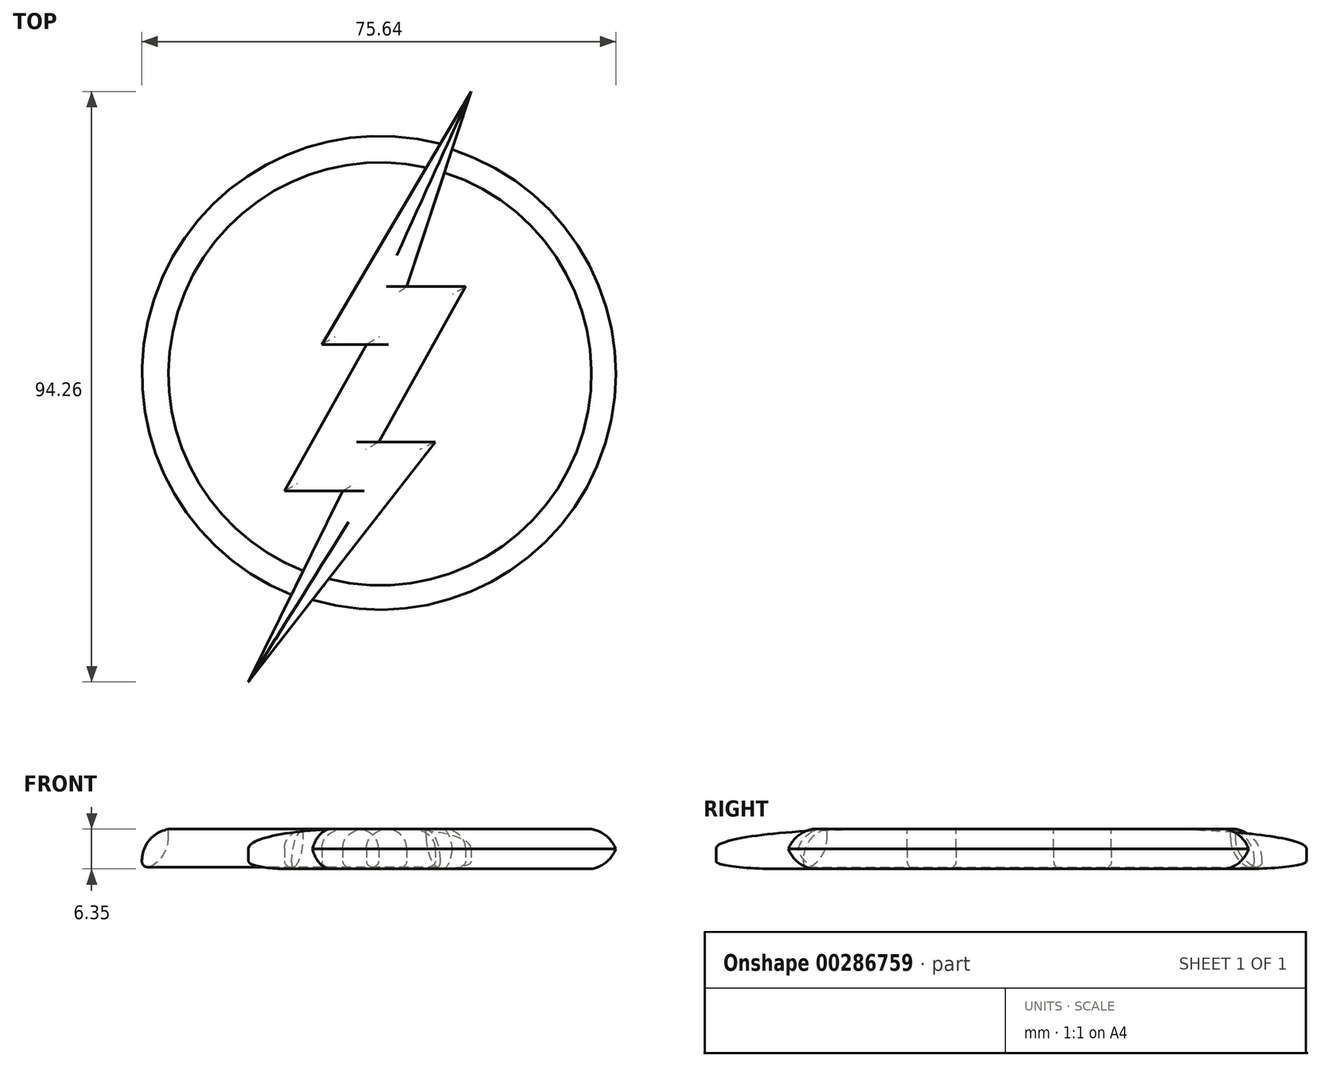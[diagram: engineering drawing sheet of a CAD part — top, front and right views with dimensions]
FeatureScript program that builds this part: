
annotation { "Feature Type Name" : "Feature", "Feature Type Description" : "" }
export const myFeature = defineFeature(function(context is Context, id is Id, definition is map)
    precondition{}
    {
        {
            var Q0;
            Q0=qCreatedBy(makeId("Top.planeOp"),FACE);
            var sketch = newSketch(context, id + "F0", { "sketchPlane" : qUnion([Q0])});
            skLineSegment(sketch, "E0", {"start": v(20.53, 51.39) * mm, "end": v(-3.33, 11.02) * mm});
            skLineSegment(sketch, "E1", {"start": v(-3.33, 11.02) * mm, "end": v(3.78, 11.02) * mm});
            skLineSegment(sketch, "E2", {"start": v(3.78, 11.02) * mm, "end": v(-9.3, -12.37) * mm});
            skLineSegment(sketch, "E3", {"start": v(-9.3, -12.37) * mm, "end": v(0, -12.37) * mm});
            skLineSegment(sketch, "E4", {"start": v(0, -12.37) * mm, "end": v(-15.02, -42.87) * mm});
            skLineSegment(sketch, "E5", {"start": v(-15.02, -42.87) * mm, "end": v(14.8, -4.57) * mm});
            skLineSegment(sketch, "E6", {"start": v(14.8, -4.57) * mm, "end": v(5.75, -4.57) * mm});
            skLineSegment(sketch, "E7", {"start": v(5.75, -4.57) * mm, "end": v(19.61, 20.24) * mm});
            skLineSegment(sketch, "E8", {"start": v(19.61, 20.24) * mm, "end": v(10.2, 20.24) * mm});
            skLineSegment(sketch, "E9", {"start": v(20.53, 51.39) * mm, "end": v(10.2, 20.24) * mm});
            skSolve(sketch);
        }
        {
            var Q0;
            Q0=qSketchRegion(id+"F0",true);
            extrude(context, id + "F1", {"entities" : qUnion([Q0]), "depth" : 6.35 * mm});
        }
        {
            var Q0;
            Q0=makeQuery(id+"F1.opExtrude","CAP_FACE",FACE,{"disambiguationData":[OSD([sQuery(id+"F0.wireOp",EDGE,"E0"),sQuery(id+"F0.wireOp",EDGE,"E1"),sQuery(id+"F0.wireOp",EDGE,"E2"),sQuery(id+"F0.wireOp",EDGE,"E3"),sQuery(id+"F0.wireOp",EDGE,"E4"),sQuery(id+"F0.wireOp",EDGE,"E5"),sQuery(id+"F0.wireOp",EDGE,"E6"),sQuery(id+"F0.wireOp",EDGE,"E7"),sQuery(id+"F0.wireOp",EDGE,"E8"),sQuery(id+"F0.wireOp",EDGE,"E9")])],"isStart":false});
            var sketch = newSketch(context, id + "F2", { "sketchPlane" : qUnion([Q0])});
            skCircle(sketch, "E10", {"center": v(5.95, 6.31) * mm, "radius": 33.75 * mm});
            skCircle(sketch, "E11", {"center": v(5.95, 6.31) * mm, "radius": 38 * mm});
            skSolve(sketch);
        }
        {
            var Q0;
            {var subQ0=sQuery(id+"F2.wireOp",EDGE,"E10");var subQ1=makeQuery(id+"F1.opExtrude","CAP_EDGE",EDGE,{"disambiguationData":[OSD([sQuery(id+"F0.wireOp",EDGE,"E0")])],"isStart":false});var subQ2=makeQuery(id+"F2.imprint","INTERSECT",VERTEX,{"derivedFrom":[subQ1,subQ0]});Q0=makeQuery(id+"F2.imprint","IMPRINT",FACE,{"disambiguationData":[TD([[makeQuery(id+"F2.imprint","IMPRINT",EDGE,{"disambiguationData":[TD([[subQ2,-1.0]])],"derivedFrom":subQ0}),-1.0]])]});}
            var Q1;
            {var subQ0=sQuery(id+"F2.wireOp",EDGE,"E10");var subQ1=makeQuery(id+"F1.opExtrude","CAP_EDGE",EDGE,{"disambiguationData":[OSD([sQuery(id+"F0.wireOp",EDGE,"E9")])],"isStart":false});var subQ2=makeQuery(id+"F2.imprint","INTERSECT",VERTEX,{"derivedFrom":[subQ1,subQ0]});Q1=makeQuery(id+"F2.imprint","IMPRINT",FACE,{"disambiguationData":[TD([[makeQuery(id+"F2.imprint","IMPRINT",EDGE,{"disambiguationData":[TD([[subQ2,1.0]])],"derivedFrom":subQ0}),-1.0]])]});}
            extrude(context, id + "F3", {"entities" : qUnion([Q0, Q1]), "oppositeDirection" : true, "depth" : 6.35 * mm});
        }
        {
            var Q0;
            {var subQ0=sQuery(id+"F2.wireOp",EDGE,"E11");Q0=makeQuery(id+"F3.opExtrude","CAP_EDGE",EDGE,{"disambiguationData":[OSD([subQ0]),TDD([makeQuery(id+"F2.imprint","IMPRINT",EDGE,{"disambiguationData":[TD([[makeQuery(id+"F2.imprint","INTERSECT",VERTEX,{"derivedFrom":[makeQuery(id+"F1.opExtrude","CAP_EDGE",EDGE,{"disambiguationData":[OSD([sQuery(id+"F0.wireOp",EDGE,"E9")])],"isStart":false}),subQ0]}),1.0]])],"derivedFrom":subQ0})])],"isStart":true});}
            var Q1;
            {var subQ0=sQuery(id+"F2.wireOp",EDGE,"E11");Q1=makeQuery(id+"F3.opExtrude","CAP_EDGE",EDGE,{"disambiguationData":[OSD([subQ0]),TDD([makeQuery(id+"F2.imprint","IMPRINT",EDGE,{"disambiguationData":[TD([[makeQuery(id+"F2.imprint","INTERSECT",VERTEX,{"derivedFrom":[makeQuery(id+"F1.opExtrude","CAP_EDGE",EDGE,{"disambiguationData":[OSD([sQuery(id+"F0.wireOp",EDGE,"E9")])],"isStart":false}),subQ0]}),1.0]])],"derivedFrom":subQ0})])],"isStart":false});}
            fillet(context, id + "F4", {"entities" : qUnion([Q0, Q1]), "radius" : 5.08 * mm, "tangentPropagation" : true, "allowEdgeOverflow" : false});
        }
        {
            var Q0;
            Q0=makeQuery(id+"F1.opExtrude","CAP_EDGE",EDGE,{"disambiguationData":[OSD([sQuery(id+"F0.wireOp",EDGE,"E2")])],"isStart":false});
            var Q1;
            Q1=makeQuery(id+"F1.opExtrude","CAP_EDGE",EDGE,{"disambiguationData":[OSD([sQuery(id+"F0.wireOp",EDGE,"E0")])],"isStart":false});
            var Q2;
            Q2=makeQuery(id+"F1.opExtrude","CAP_EDGE",EDGE,{"disambiguationData":[OSD([sQuery(id+"F0.wireOp",EDGE,"E7")])],"isStart":false});
            var Q3;
            Q3=makeQuery(id+"F1.opExtrude","CAP_EDGE",EDGE,{"disambiguationData":[OSD([sQuery(id+"F0.wireOp",EDGE,"E5")])],"isStart":false});
            var Q4;
            Q4=makeQuery(id+"F1.opExtrude","CAP_EDGE",EDGE,{"disambiguationData":[OSD([sQuery(id+"F0.wireOp",EDGE,"E4")])],"isStart":false});
            var Q5;
            Q5=makeQuery(id+"F1.opExtrude","CAP_EDGE",EDGE,{"disambiguationData":[OSD([sQuery(id+"F0.wireOp",EDGE,"E9")])],"isStart":false});
            fillet(context, id + "F5", {"entities" : qUnion([Q0, Q1, Q2, Q3, Q4, Q5]), "radius" : 3.07 * mm, "tangentPropagation" : true, "allowEdgeOverflow" : false});
        }
        {
            var Q0;
            {var subQ0=sQuery(id+"F2.wireOp",EDGE,"E10");Q0=makeQuery(id+"F3.opExtrude","CAP_EDGE",EDGE,{"disambiguationData":[OSD([subQ0]),TDD([makeQuery(id+"F2.imprint","IMPRINT",EDGE,{"disambiguationData":[TD([[makeQuery(id+"F2.imprint","INTERSECT",VERTEX,{"derivedFrom":[makeQuery(id+"F1.opExtrude","CAP_EDGE",EDGE,{"disambiguationData":[OSD([sQuery(id+"F0.wireOp",EDGE,"E0")])],"isStart":false}),subQ0]}),-1.0]])],"derivedFrom":subQ0})])],"isStart":false});}
            var Q1;
            {var subQ0=sQuery(id+"F2.wireOp",EDGE,"E11");Q1=makeQuery(id+"F3.opExtrude","CAP_EDGE",EDGE,{"disambiguationData":[OSD([subQ0]),TDD([makeQuery(id+"F2.imprint","IMPRINT",EDGE,{"disambiguationData":[TD([[makeQuery(id+"F2.imprint","INTERSECT",VERTEX,{"derivedFrom":[makeQuery(id+"F1.opExtrude","CAP_EDGE",EDGE,{"disambiguationData":[OSD([sQuery(id+"F0.wireOp",EDGE,"E0")])],"isStart":false}),subQ0]}),-1.0]])],"derivedFrom":subQ0})])],"isStart":true});}
            fillet(context, id + "F6", {"entities" : qUnion([Q0, Q1]), "radius" : 5.08 * mm, "tangentPropagation" : true, "allowEdgeOverflow" : false});
        }
        {
            var Q0;
            {var subQ0=sQuery(id+"F2.wireOp",EDGE,"E11");var subQ1=makeQuery(id+"F1.opExtrude","CAP_EDGE",EDGE,{"disambiguationData":[OSD([sQuery(id+"F0.wireOp",EDGE,"E0")])],"isStart":false});var subQ3=sQuery(id+"F2.wireOp",EDGE,"E10");Q0=makeQuery(id+"F6.opFillet","BLEND_EDGE",EDGE,{"blendedFrom":[makeQuery(id+"F3.opExtrude","CAP_EDGE",EDGE,{"disambiguationData":[OSD([subQ3]),TDD([makeQuery(id+"F2.imprint","IMPRINT",EDGE,{"disambiguationData":[TD([[makeQuery(id+"F2.imprint","INTERSECT",VERTEX,{"derivedFrom":[subQ1,subQ3]}),-1.0]])],"derivedFrom":subQ3})])],"isStart":false}),makeQuery(id+"F3.opExtrude","SWEPT_FACE",FACE,{"disambiguationData":[OSD([subQ0]),TDD([makeQuery(id+"F2.imprint","IMPRINT",EDGE,{"disambiguationData":[TD([[makeQuery(id+"F2.imprint","INTERSECT",VERTEX,{"derivedFrom":[subQ1,subQ0]}),-1.0]])],"derivedFrom":subQ0})])]})],"blendedInto":[makeQuery(id+"F3.opExtrude","SWEPT_FACE",FACE,{"disambiguationData":[OSD([subQ0]),TDD([makeQuery(id+"F2.imprint","IMPRINT",EDGE,{"disambiguationData":[TD([[makeQuery(id+"F2.imprint","INTERSECT",VERTEX,{"derivedFrom":[subQ1,subQ0]}),-1.0]])],"derivedFrom":subQ0})])]})]});}
            fillet(context, id + "F7", {"entities" : qUnion([Q0]), "radius" : 0.88 * mm, "tangentPropagation" : true, "allowEdgeOverflow" : false});
        }
        {
            var Q0;
            Q0=makeQuery(id+"F1.opExtrude","CAP_EDGE",EDGE,{"disambiguationData":[OSD([sQuery(id+"F0.wireOp",EDGE,"E4")])],"isStart":true});
            var Q1;
            Q1=makeQuery(id+"F1.opExtrude","CAP_EDGE",EDGE,{"disambiguationData":[OSD([sQuery(id+"F0.wireOp",EDGE,"E5")])],"isStart":true});
            var Q2;
            Q2=makeQuery(id+"F1.opExtrude","CAP_EDGE",EDGE,{"disambiguationData":[OSD([sQuery(id+"F0.wireOp",EDGE,"E3")])],"isStart":true});
            var Q3;
            Q3=makeQuery(id+"F1.opExtrude","CAP_EDGE",EDGE,{"disambiguationData":[OSD([sQuery(id+"F0.wireOp",EDGE,"E2")])],"isStart":true});
            var Q4;
            Q4=makeQuery(id+"F1.opExtrude","CAP_EDGE",EDGE,{"disambiguationData":[OSD([sQuery(id+"F0.wireOp",EDGE,"E7")])],"isStart":true});
            var Q5;
            Q5=makeQuery(id+"F1.opExtrude","CAP_EDGE",EDGE,{"disambiguationData":[OSD([sQuery(id+"F0.wireOp",EDGE,"E6")])],"isStart":true});
            var Q6;
            Q6=makeQuery(id+"F1.opExtrude","CAP_EDGE",EDGE,{"disambiguationData":[OSD([sQuery(id+"F0.wireOp",EDGE,"E1")])],"isStart":true});
            var Q7;
            Q7=makeQuery(id+"F1.opExtrude","CAP_EDGE",EDGE,{"disambiguationData":[OSD([sQuery(id+"F0.wireOp",EDGE,"E8")])],"isStart":true});
            var Q8;
            Q8=makeQuery(id+"F1.opExtrude","CAP_EDGE",EDGE,{"disambiguationData":[OSD([sQuery(id+"F0.wireOp",EDGE,"E0")])],"isStart":true});
            var Q9;
            Q9=makeQuery(id+"F1.opExtrude","CAP_EDGE",EDGE,{"disambiguationData":[OSD([sQuery(id+"F0.wireOp",EDGE,"E9")])],"isStart":true});
            fillet(context, id + "F8", {"entities" : qUnion([Q0, Q1, Q2, Q3, Q4, Q5, Q6, Q7, Q8, Q9]), "radius" : 1.23 * mm, "tangentPropagation" : true, "allowEdgeOverflow" : false});
        }
    });
